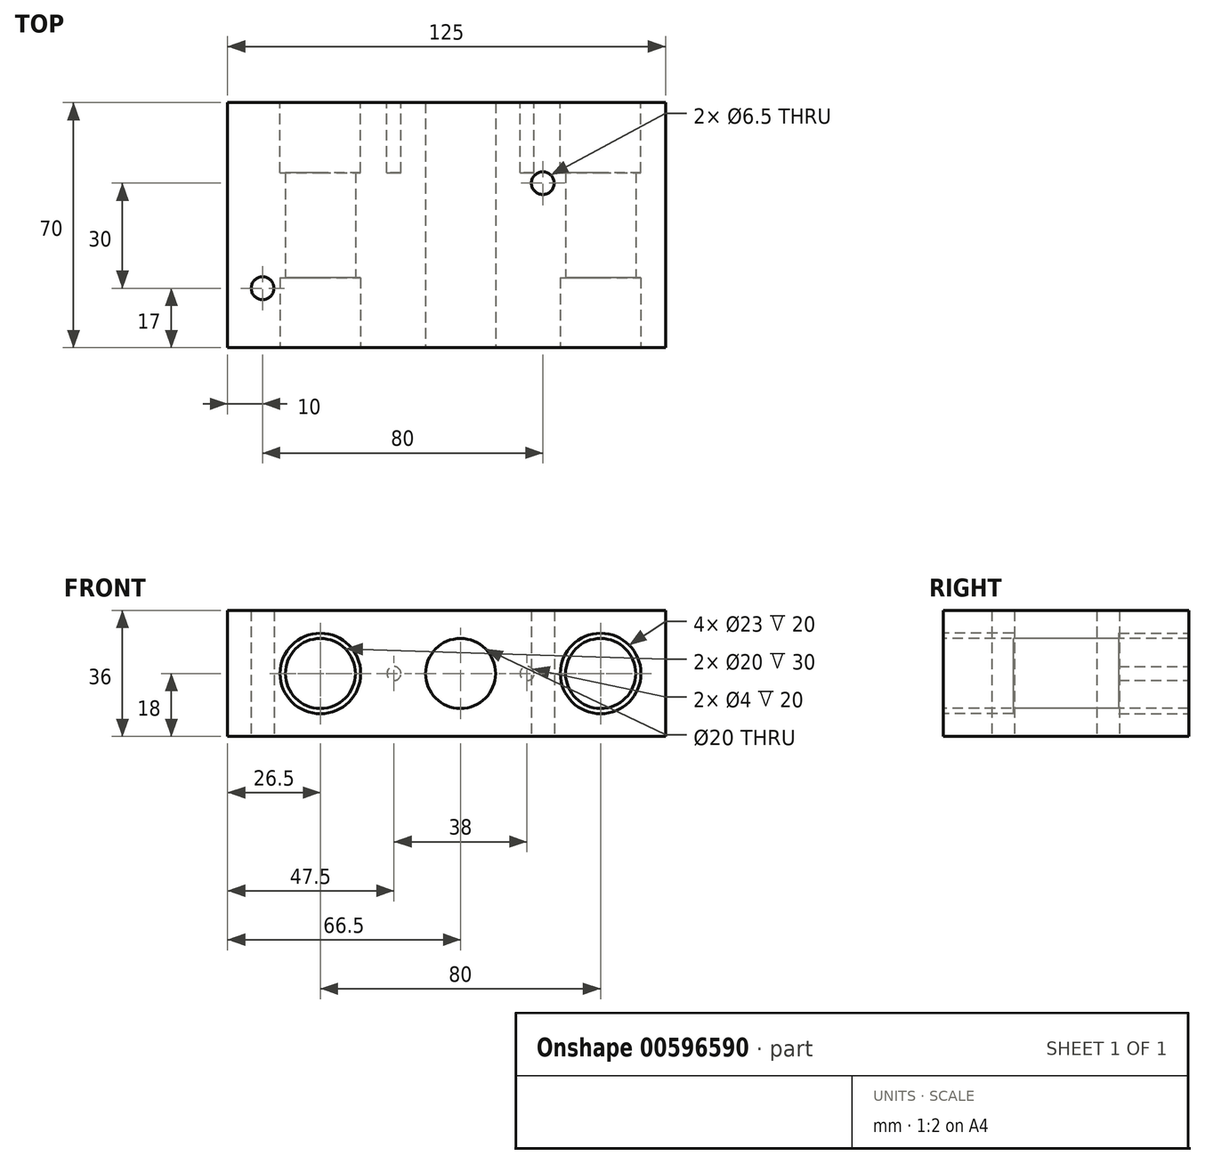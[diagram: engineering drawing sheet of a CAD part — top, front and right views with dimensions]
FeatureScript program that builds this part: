
annotation { "Feature Type Name" : "Feature", "Feature Type Description" : "" }
export const myFeature = defineFeature(function(context is Context, id is Id, definition is map)
    precondition{}
    {
        {
            var Q0;
            Q0=qCreatedBy(makeId("Top.planeOp"),FACE);
            var sketch = newSketch(context, id + "F0", { "sketchPlane" : qUnion([Q0])});
            skLineSegment(sketch, "E0.bottom", {"start": v(0, 0) * mm, "end": v(125, 0) * mm});
            skLineSegment(sketch, "E0.top", {"start": v(0, 70) * mm, "end": v(125, 70) * mm});
            skLineSegment(sketch, "E0.left", {"start": v(0, 0) * mm, "end": v(0, 70) * mm});
            skLineSegment(sketch, "E0.right", {"start": v(125, 0) * mm, "end": v(125, 70) * mm});
            skSolve(sketch);
        }
        {
            var Q0;
            Q0=makeQuery(id+"F0.imprint","IMPRINT",FACE,{"disambiguationData":[TD([[makeQuery(id+"F0.imprint","IMPRINT",EDGE,{"derivedFrom":sQuery(id+"F0.wireOp",EDGE,"E0.bottom")}),1.0]])]});
            extrude(context, id + "F1", {"entities" : qUnion([Q0]), "depth" : 36 * mm, "offsetDistance" : 25 * mm});
        }
        {
            var Q0;
            Q0=makeQuery(id+"F1.opExtrude","SWEPT_FACE",FACE,{"disambiguationData":[OSD([sQuery(id+"F0.wireOp",EDGE,"E0.bottom")])]});
            var sketch = newSketch(context, id + "F2", { "sketchPlane" : qUnion([Q0])});
            skCircle(sketch, "E1", {"center": v(26.5, 18) * mm, "radius": 10 * mm});
            skCircle(sketch, "E2", {"center": v(66.5, 18) * mm, "radius": 10 * mm});
            skCircle(sketch, "E3", {"center": v(106.5, 18) * mm, "radius": 10 * mm});
            skSolve(sketch);
        }
        {
            var Q0;
            Q0=qSketchRegion(id+"F2",true);
            extrude(context, id + "F3", {"entities" : qUnion([Q0]), "operationType" : NewBodyOperationType.REMOVE, "endBound" : BoundingType.THROUGH_ALL, "oppositeDirection" : true, "depth" : 25 * mm, "offsetDistance" : 25 * mm});
        }
        {
            var Q0;
            Q0=makeQuery(id+"F1.opExtrude","SWEPT_FACE",FACE,{"disambiguationData":[OSD([sQuery(id+"F0.wireOp",EDGE,"E0.bottom")])]});
            var sketch = newSketch(context, id + "F4", { "sketchPlane" : qUnion([Q0])});
            skCircle(sketch, "E4", {"center": v(26.5, 18) * mm, "radius": 11.5 * mm});
            skCircle(sketch, "E5", {"center": v(106.5, 18) * mm, "radius": 11.5 * mm});
            skSolve(sketch);
        }
        {
            var Q0;
            Q0=makeQuery(id+"F4.imprint","IMPRINT",FACE,{"disambiguationData":[TD([[makeQuery(id+"F4.imprint","IMPRINT",EDGE,{"derivedFrom":sQuery(id+"F4.wireOp",EDGE,"E4")}),1.0]])]});
            var Q1;
            Q1=makeQuery(id+"F4.imprint","IMPRINT",FACE,{"disambiguationData":[TD([[makeQuery(id+"F4.imprint","IMPRINT",EDGE,{"derivedFrom":sQuery(id+"F4.wireOp",EDGE,"E5")}),1.0]])]});
            extrude(context, id + "F5", {"entities" : qUnion([Q0, Q1]), "operationType" : NewBodyOperationType.REMOVE, "oppositeDirection" : true, "depth" : 20 * mm, "offsetDistance" : 25 * mm});
        }
        {
            var Q0;
            Q0=makeQuery(id+"F1.opExtrude","SWEPT_FACE",FACE,{"disambiguationData":[OSD([sQuery(id+"F0.wireOp",EDGE,"E0.top")])]});
            var sketch = newSketch(context, id + "F6", { "sketchPlane" : qUnion([Q0])});
            skCircle(sketch, "E6", {"center": v(-106.5, 18) * mm, "radius": 11.5 * mm});
            skCircle(sketch, "E7", {"center": v(-26.5, 18) * mm, "radius": 11.5 * mm});
            skSolve(sketch);
        }
        {
            var Q0;
            Q0=makeQuery(id+"F6.imprint","IMPRINT",FACE,{"disambiguationData":[TD([[makeQuery(id+"F6.imprint","IMPRINT",EDGE,{"derivedFrom":sQuery(id+"F6.wireOp",EDGE,"E6")}),1.0]])]});
            var Q1;
            Q1=makeQuery(id+"F6.imprint","IMPRINT",FACE,{"disambiguationData":[TD([[makeQuery(id+"F6.imprint","IMPRINT",EDGE,{"derivedFrom":sQuery(id+"F6.wireOp",EDGE,"E7")}),1.0]])]});
            extrude(context, id + "F7", {"entities" : qUnion([Q0, Q1]), "operationType" : NewBodyOperationType.REMOVE, "oppositeDirection" : true, "depth" : 20 * mm, "offsetDistance" : 25 * mm});
        }
        {
            var Q0;
            Q0=makeQuery(id+"F1.opExtrude","CAP_FACE",FACE,{"disambiguationData":[OSD([sQuery(id+"F0.wireOp",EDGE,"E0.bottom"),sQuery(id+"F0.wireOp",EDGE,"E0.top"),sQuery(id+"F0.wireOp",EDGE,"E0.left"),sQuery(id+"F0.wireOp",EDGE,"E0.right")])],"isStart":true});
            var sketch = newSketch(context, id + "F8", { "sketchPlane" : qUnion([Q0])});
            skLineSegment(sketch, "E8", {"start": v(0, -35) * mm, "end": v(22.85, -35) * mm, "construction": true});
            skCircle(sketch, "E9.MirrorC", {"center": v(10, -17) * mm, "radius": 3.25 * mm});
            skCircle(sketch, "E10.MirrorC", {"center": v(90, -47) * mm, "radius": 3.25 * mm});
            skSolve(sketch);
        }
        {
            var Q0;
            Q0=qSketchRegion(id+"F8",true);
            extrude(context, id + "F9", {"entities" : qUnion([Q0]), "operationType" : NewBodyOperationType.REMOVE, "endBound" : BoundingType.THROUGH_ALL, "oppositeDirection" : true, "depth" : 25 * mm, "offsetDistance" : 25 * mm});
        }
        {
            var Q0;
            Q0=makeQuery(id+"F1.opExtrude","SWEPT_FACE",FACE,{"disambiguationData":[OSD([sQuery(id+"F0.wireOp",EDGE,"E0.top")])]});
            var sketch = newSketch(context, id + "F10", { "sketchPlane" : qUnion([Q0])});
            skCircle(sketch, "E11", {"center": v(-66.5, 18) * mm, "radius": 19 * mm, "construction": true});
            skCircle(sketch, "E12", {"center": v(-85.5, 18) * mm, "radius": 2 * mm});
            skCircle(sketch, "E13", {"center": v(-47.5, 18) * mm, "radius": 2 * mm});
            skSolve(sketch);
        }
        {
            var Q0;
            Q0=makeQuery(id+"F10.imprint","IMPRINT",FACE,{"disambiguationData":[TD([[makeQuery(id+"F10.imprint","IMPRINT",EDGE,{"derivedFrom":sQuery(id+"F10.wireOp",EDGE,"E12")}),1.0]])]});
            var Q1;
            Q1=makeQuery(id+"F10.imprint","IMPRINT",FACE,{"disambiguationData":[TD([[makeQuery(id+"F10.imprint","IMPRINT",EDGE,{"derivedFrom":sQuery(id+"F10.wireOp",EDGE,"E13")}),1.0]])]});
            extrude(context, id + "F11", {"entities" : qUnion([Q0, Q1]), "operationType" : NewBodyOperationType.REMOVE, "oppositeDirection" : true, "depth" : 20 * mm, "offsetDistance" : 25 * mm});
        }
    });
